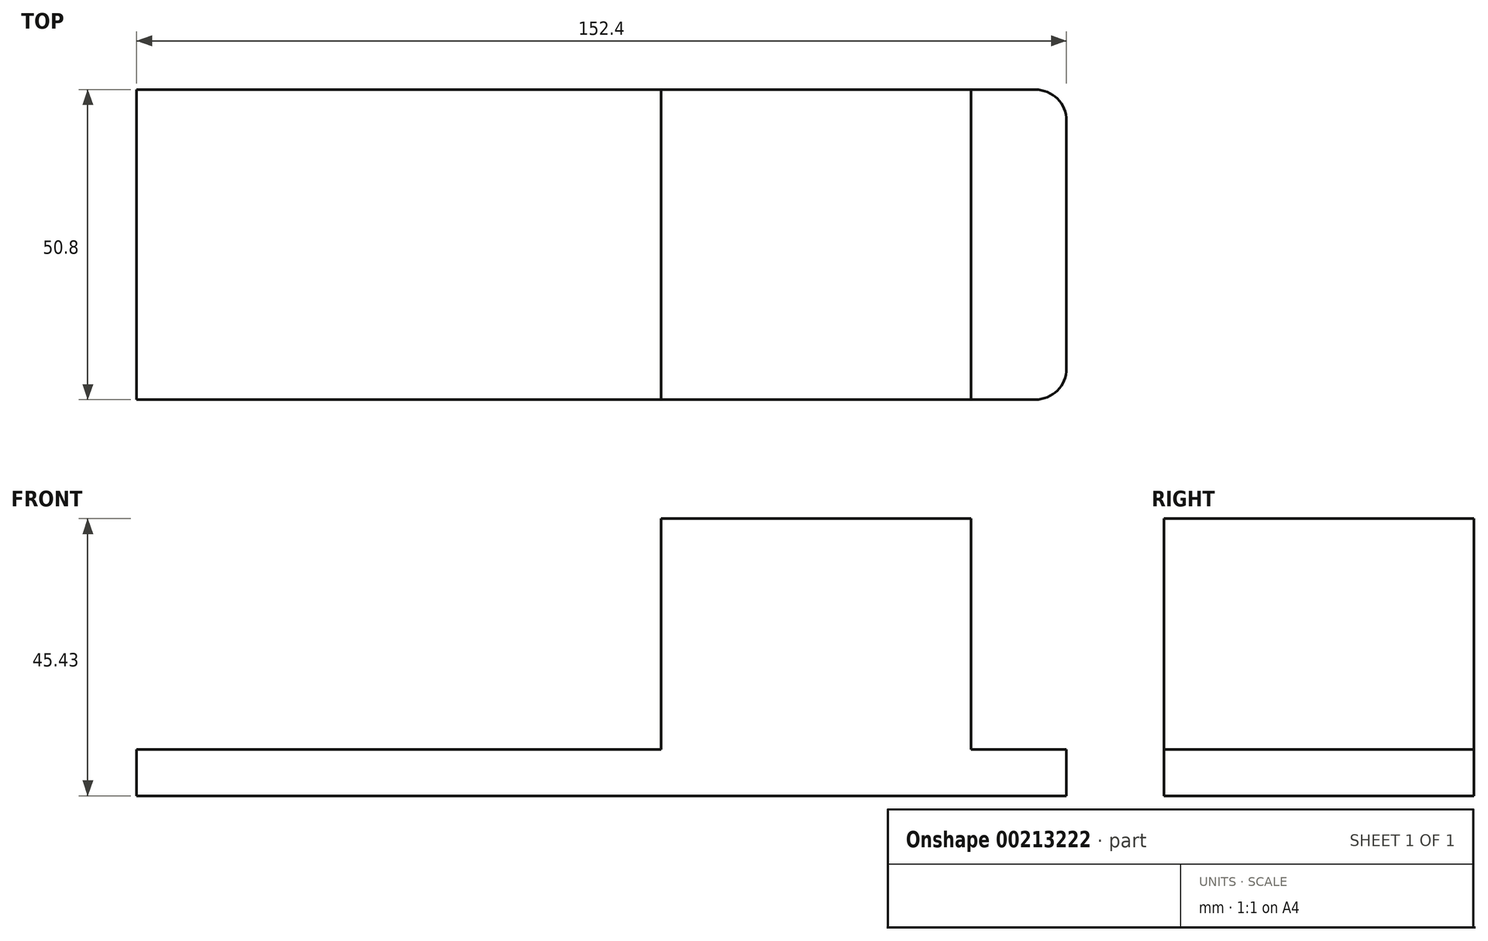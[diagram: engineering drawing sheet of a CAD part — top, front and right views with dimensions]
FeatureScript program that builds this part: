
annotation { "Feature Type Name" : "Feature", "Feature Type Description" : "" }
export const myFeature = defineFeature(function(context is Context, id is Id, definition is map)
    precondition{}
    {
        {
            var Q0;
            Q0=qCreatedBy(makeId("Front.planeOp"),FACE);
            var sketch = newSketch(context, id + "F0", { "sketchPlane" : qUnion([Q0])});
            skLineSegment(sketch, "E0.bottom", {"start": v(-25.4, 19.05) * mm, "end": v(25.4, 19.05) * mm});
            skLineSegment(sketch, "E0.top", {"start": v(-25.4, -19.05) * mm, "end": v(25.4, -19.05) * mm});
            skLineSegment(sketch, "E0.left", {"start": v(-25.4, 19.05) * mm, "end": v(-25.4, -19.05) * mm});
            skLineSegment(sketch, "E0.right", {"start": v(25.4, 19.05) * mm, "end": v(25.4, -19.05) * mm});
            skPoint(sketch, "E0.middle", {"position": v(0, 0) * mm});
            skLineSegment(sketch, "E1.bottom", {"start": v(41.05, -18.76) * mm, "end": v(-111.35, -18.76) * mm});
            skLineSegment(sketch, "E1.top", {"start": v(41.05, -26.38) * mm, "end": v(-111.35, -26.38) * mm});
            skLineSegment(sketch, "E1.left", {"start": v(41.05, -18.76) * mm, "end": v(41.05, -26.38) * mm});
            skLineSegment(sketch, "E1.right", {"start": v(-111.35, -18.76) * mm, "end": v(-111.35, -26.38) * mm});
            skSolve(sketch);
        }
        {
            var Q0;
            Q0 = qSketchRegion(id + "F0", true);
            extrude(context, id + "F1", {"entities" : qUnion([Q0]), "depth" : 50.8 * mm});
        }
        {
            var Q0;
            Q0=makeQuery(id+"F1.opExtrude","CAP_EDGE",EDGE,{"disambiguationData":[OSD([sQuery(id+"F0.wireOp",EDGE,"E1.left")])],"isStart":true});
            var Q1;
            Q1=makeQuery(id+"F1.opExtrude","CAP_EDGE",EDGE,{"disambiguationData":[OSD([sQuery(id+"F0.wireOp",EDGE,"E1.left")])],"isStart":false});
            fillet(context, id + "F2", {"entities" : qUnion([Q0, Q1]), "radius" : 5.08 * mm, "tangentPropagation" : true, "allowEdgeOverflow" : false});
        }
    });
